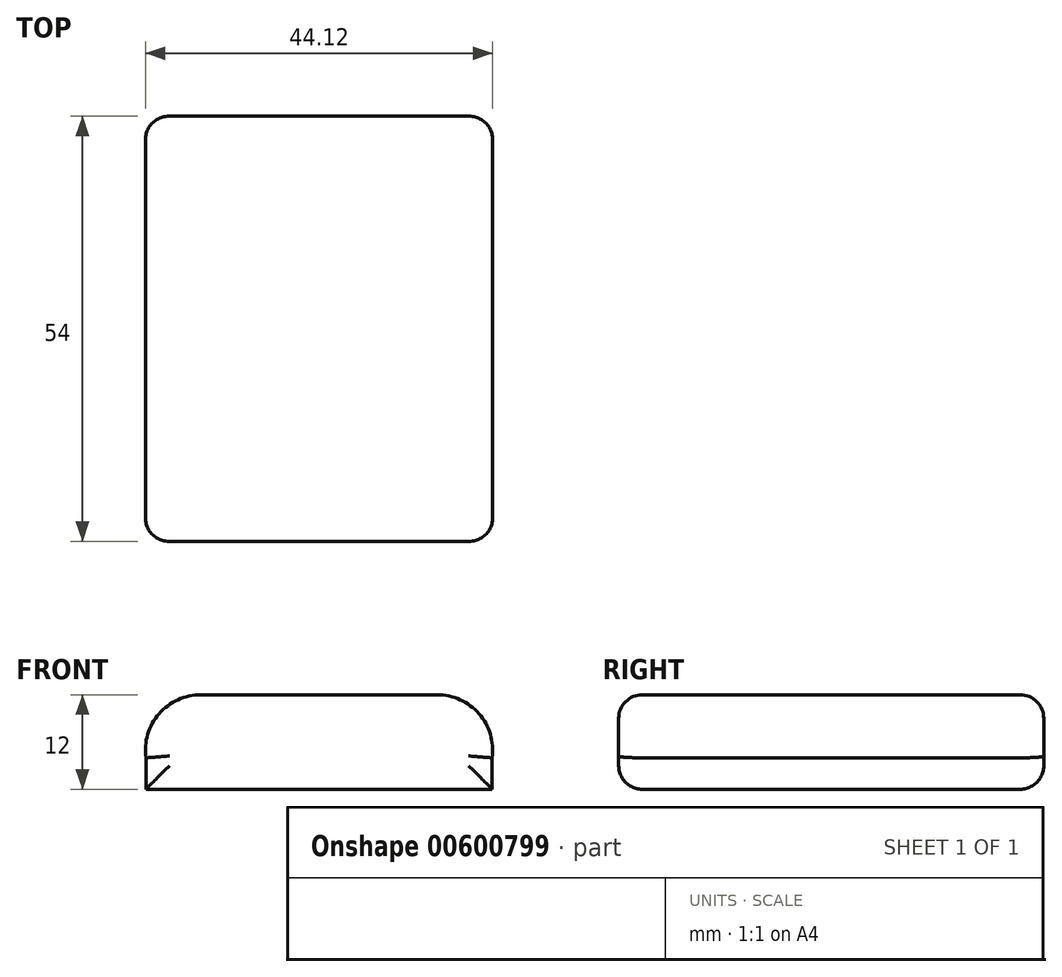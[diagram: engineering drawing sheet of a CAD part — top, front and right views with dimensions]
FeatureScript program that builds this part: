
annotation { "Feature Type Name" : "Feature", "Feature Type Description" : "" }
export const myFeature = defineFeature(function(context is Context, id is Id, definition is map)
    precondition{}
    {
        {
            var Q0;
            Q0=qCreatedBy(makeId("Front.planeOp"),FACE);
            var sketch = newSketch(context, id + "F0", { "sketchPlane" : qUnion([Q0])});
            skLineSegment(sketch, "E0.bottom", {"start": v(15, -6) * mm, "end": v(-15, -6) * mm});
            skLineSegment(sketch, "E0.top", {"start": v(15, 6) * mm, "end": v(-15, 6) * mm});
            skLineSegment(sketch, "E0.left", {"start": v(15, -6) * mm, "end": v(15, 6) * mm});
            skLineSegment(sketch, "E0.right", {"start": v(-15, -6) * mm, "end": v(-15, 6) * mm});
            skPoint(sketch, "E0.middle", {"position": v(0, 0) * mm});
            skLineSegment(sketch, "E1", {"start": v(-15, -6) * mm, "end": v(-22, -6) * mm});
            skLineSegment(sketch, "E2", {"start": v(15, -6) * mm, "end": v(22, -6) * mm});
            skLineSegment(sketch, "E3", {"start": v(-22, -6) * mm, "end": v(-22, -2) * mm});
            skLineSegment(sketch, "E4", {"start": v(22, -6) * mm, "end": v(22, -2) * mm});
            skArc(sketch, "E5", {"start": v(-15, 6) * mm, "mid": v(-20.32, 3.59) * mm, "end": v(-22, -2) * mm});
            skArc(sketch, "E6", {"start": v(22, -2) * mm, "mid": v(20.32, 3.59) * mm, "end": v(15, 6) * mm});
            skSolve(sketch);
        }
        {
            var Q0;
            Q0=qSketchRegion(id+"F0",true);
            extrude(context, id + "F1", {"entities" : qUnion([Q0]), "depth" : 54 * mm, "offsetDistance" : 25 * mm});
        }
        {
            var Q0;
            Q0=makeQuery(id+"F1.opExtrude","CAP_FACE",FACE,{"disambiguationData":[OSD([sQuery(id+"F0.wireOp",EDGE,"E0.bottom"),sQuery(id+"F0.wireOp",EDGE,"E0.top"),sQuery(id+"F0.wireOp",EDGE,"E1"),sQuery(id+"F0.wireOp",EDGE,"E2"),sQuery(id+"F0.wireOp",EDGE,"E3"),sQuery(id+"F0.wireOp",EDGE,"E4"),sQuery(id+"F0.wireOp",EDGE,"stta9PV9-G0h3-lKJE-htm5-4mhzk5wmezgI"),sQuery(id+"F0.wireOp",EDGE,"O8ZtQp2x-5TGG-lX6x-Sl6Y-NY4k2NN79q24")])],"isStart":false});
            fillet(context, id + "F2", {"entities" : qUnion([Q0]), "radius" : 3 * mm, "tangentPropagation" : true, "allowEdgeOverflow" : false});
        }
        {
            var Q0;
            Q0=makeQuery(id+"F1.opExtrude","CAP_FACE",FACE,{"disambiguationData":[OSD([sQuery(id+"F0.wireOp",EDGE,"E0.bottom"),sQuery(id+"F0.wireOp",EDGE,"E0.top"),sQuery(id+"F0.wireOp",EDGE,"E1"),sQuery(id+"F0.wireOp",EDGE,"E2"),sQuery(id+"F0.wireOp",EDGE,"E3"),sQuery(id+"F0.wireOp",EDGE,"E4"),sQuery(id+"F0.wireOp",EDGE,"E5"),sQuery(id+"F0.wireOp",EDGE,"E6")])],"isStart":true});
            fillet(context, id + "F3", {"entities" : qUnion([Q0]), "radius" : 3 * mm, "tangentPropagation" : true, "allowEdgeOverflow" : false});
        }
    });
